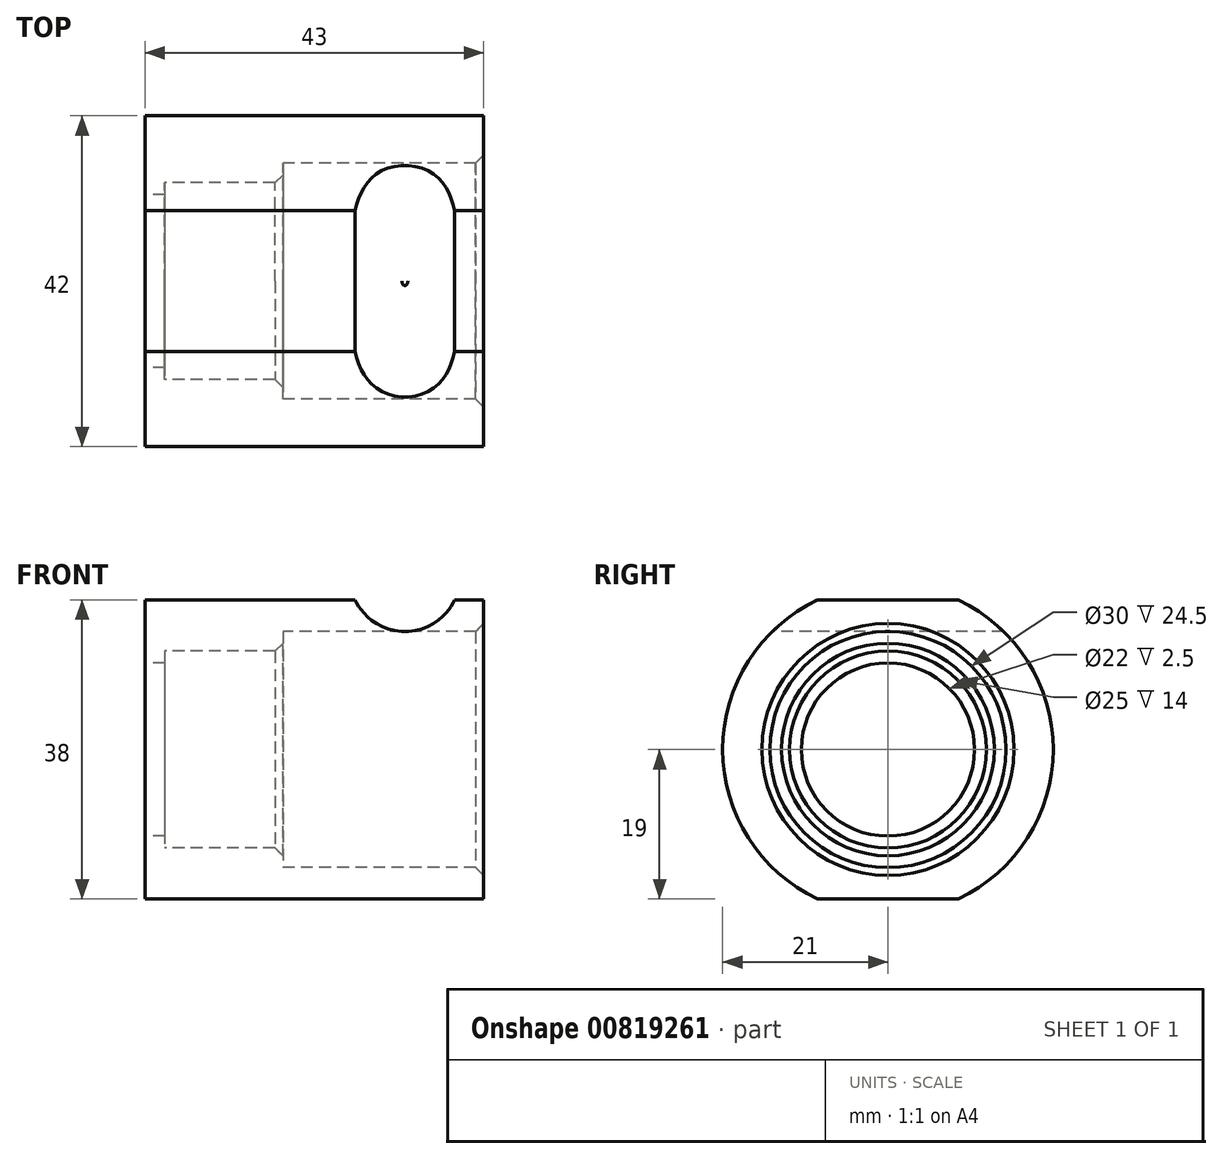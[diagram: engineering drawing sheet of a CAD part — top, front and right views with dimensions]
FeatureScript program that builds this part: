
annotation { "Feature Type Name" : "Feature", "Feature Type Description" : "" }
export const myFeature = defineFeature(function(context is Context, id is Id, definition is map)
    precondition{}
    {
        {
            var Q0;
            Q0=qCreatedBy(makeId("Front.planeOp"),FACE);
            var sketch = newSketch(context, id + "F0", { "sketchPlane" : qUnion([Q0])});
            skLineSegment(sketch, "E0", {"start": v(43, 21) * mm, "end": v(0, 21) * mm});
            skLineSegment(sketch, "E1", {"start": v(2.5, 12.5) * mm, "end": v(17.5, 12.5) * mm});
            skLineSegment(sketch, "E2", {"start": v(17.5, 15) * mm, "end": v(43, 15) * mm});
            skLineSegment(sketch, "E3", {"start": v(43, 15) * mm, "end": v(43, 21) * mm});
            skLineSegment(sketch, "E4", {"start": v(17.5, 15) * mm, "end": v(17.5, 12.5) * mm});
            skLineSegment(sketch, "E5", {"start": v(-37.37, 0) * mm, "end": v(57.45, 0) * mm, "construction": true});
            skLineSegment(sketch, "E6", {"start": v(2.5, 12.5) * mm, "end": v(2.5, 11) * mm});
            skLineSegment(sketch, "E7", {"start": v(2.5, 11) * mm, "end": v(0, 11) * mm});
            skLineSegment(sketch, "E8", {"start": v(0, 11) * mm, "end": v(0, 21) * mm});
            skSolve(sketch);
        }
        {
            var Q0;
            Q0=makeQuery(id+"F0.imprint","IMPRINT",FACE,{"disambiguationData":[TD([[makeQuery(id+"F0.imprint","IMPRINT",EDGE,{"derivedFrom":sQuery(id+"F0.wireOp",EDGE,"E0")}),1.0]])]});
            var Q1;
            Q1=sQuery(id+"F0.wireOp",EDGE,"E5");
            revolve(context, id + "F1", {"surfaceOperationType" : NewSurfaceOperationType.NEW, "entities" : qUnion([Q0]), "axis" : qUnion([Q1]), "revolveType" : RevolveType.FULL});
        }
        {
            var Q0;
            Q0=qCreatedBy(makeId("Front.planeOp"),FACE);
            cPlane(context, id + "F2", {"entities" : qUnion([Q0]), "cplaneType" : CPlaneType.OFFSET, "offset" : 50 * mm, "width" : 150 * mm, "height" : 150 * mm});
        }
        {
            var Q0;
            Q0=qCreatedBy(id+"F2.planeOp",FACE);
            var sketch = newSketch(context, id + "F3", { "sketchPlane" : qUnion([Q0])});
            skPoint(sketch, "E9", {"position": v(10, 0) * mm});
            skPoint(sketch, "E10", {"position": v(33, 0) * mm});
            skSolve(sketch);
        }
        {
            var Q0;
            Q0=makeQuery(id+"F1.opRevolve","SWEPT_EDGE",EDGE,{"disambiguationData":[OSD([sQuery(id+"F0.wireOp",EDGE,"E2"),sQuery(id+"F0.wireOp",EDGE,"E3")])]});
            var Q1;
            Q1=makeQuery(id+"F1.opRevolve","SWEPT_EDGE",EDGE,{"disambiguationData":[OSD([sQuery(id+"F0.wireOp",EDGE,"E1"),sQuery(id+"F0.wireOp",EDGE,"E4")])]});
            var Q2;
            Q2=makeQuery(id+"F1.opRevolve","SWEPT_EDGE",EDGE,{"disambiguationData":[OSD([sQuery(id+"F0.wireOp",EDGE,"E1"),sQuery(id+"F0.wireOp",EDGE,"E4")])]});
            chamfer(context, id + "F4", {"entities" : qUnion([Q0, Q1, Q2]), "width" : 1 * mm, "tangentPropagation" : true});
        }
        {
            var Q0;
            Q0=qCreatedBy(makeId("Front.planeOp"),FACE);
            var sketch = newSketch(context, id + "F5", { "sketchPlane" : qUnion([Q0])});
            skLineSegment(sketch, "E11.bottom", {"start": v(43, 22) * mm, "end": v(0, 22) * mm});
            skLineSegment(sketch, "E11.top", {"start": v(43, 19) * mm, "end": v(0, 19) * mm});
            skLineSegment(sketch, "E11.left", {"start": v(43, 22) * mm, "end": v(43, 19) * mm});
            skLineSegment(sketch, "E11.right", {"start": v(0, 22) * mm, "end": v(0, 19) * mm});
            skLineSegment(sketch, "E12.MirrorCS", {"start": v(43, -19) * mm, "end": v(0, -19) * mm});
            skLineSegment(sketch, "E13.MirrorCS", {"start": v(43, -22) * mm, "end": v(0, -22) * mm});
            skLineSegment(sketch, "E14.MirrorCS", {"start": v(0, -22) * mm, "end": v(0, -19) * mm});
            skLineSegment(sketch, "E15.MirrorCS", {"start": v(43, -22) * mm, "end": v(43, -19) * mm});
            skSolve(sketch);
        }
        {
            var Q0;
            Q0=makeQuery(id+"F5.imprint","IMPRINT",FACE,{"disambiguationData":[TD([[makeQuery(id+"F5.imprint","IMPRINT",EDGE,{"derivedFrom":sQuery(id+"F5.wireOp",EDGE,"E11.bottom")}),1.0]])]});
            var Q1;
            Q1=makeQuery(id+"F5.imprint","IMPRINT",FACE,{"disambiguationData":[TD([[makeQuery(id+"F5.imprint","IMPRINT",EDGE,{"derivedFrom":sQuery(id+"F5.wireOp",EDGE,"E12.MirrorCS")}),1.0]])]});
            extrude(context, id + "F6", {"entities" : qUnion([Q0, Q1]), "operationType" : NewBodyOperationType.REMOVE, "endBound" : BoundingType.THROUGH_ALL, "depth" : 25 * mm, "offsetDistance" : 25 * mm, "hasSecondDirection" : true, "secondDirectionBound" : SecondDirectionBoundingType.THROUGH_ALL, "secondDirectionOppositeDirection" : true, "secondDirectionDepth" : 25 * mm});
        }
        {
            var Q0;
            Q0=qCreatedBy(id+"F2.planeOp",FACE);
            var sketch = newSketch(context, id + "F7", { "sketchPlane" : qUnion([Q0])});
            skCircle(sketch, "E16", {"center": v(33, 21.99) * mm, "radius": 7 * mm});
            skSolve(sketch);
        }
        {
            var Q0;
            Q0=makeQuery(id+"F7.imprint","IMPRINT",FACE,{"disambiguationData":[TD([[makeQuery(id+"F7.imprint","IMPRINT",EDGE,{"derivedFrom":sQuery(id+"F7.wireOp",EDGE,"E16")}),1.0]])]});
            extrude(context, id + "F8", {"entities" : qUnion([Q0]), "operationType" : NewBodyOperationType.REMOVE, "endBound" : BoundingType.THROUGH_ALL, "oppositeDirection" : true, "depth" : 25 * mm, "offsetDistance" : 25 * mm});
        }
    });
